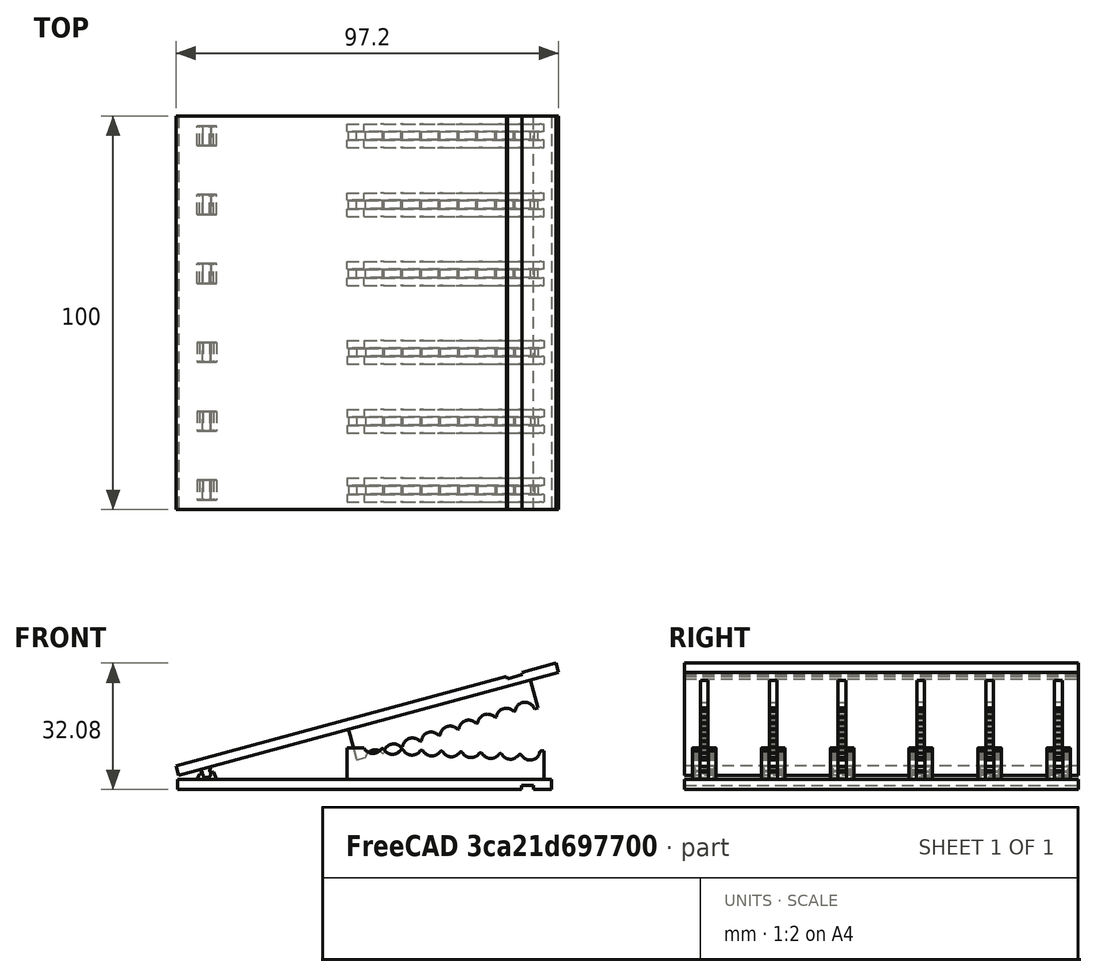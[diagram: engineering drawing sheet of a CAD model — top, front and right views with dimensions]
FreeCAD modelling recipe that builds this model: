
FCSTD DOCUMENT  (FreeCAD 2020.12.17R23076 +3024 (Git))
Label: Modular Ramp v3 Simulated
License: All rights reserved
LicenseURL: http://en.wikipedia.org/wiki/All_rights_reserved
objects: Sketcher::SketchObject×12, PartDesign::Pad×6, PartDesign::ShapeBinder×3, PartDesign::Plane×3, PartDesign::Body×3, PartDesign::Pocket×3, PartDesign::LinearPattern×2, PartDesign::Mirrored×2, Spreadsheet::Sheet×1, TechDraw::DrawSVGTemplate×1, TechDraw::DrawPage×1
note: 56 computed .brp shape members not serialized (recipe doc carries the construction recipe); baked Part::Feature solids carry a one-line shape summary decoded from their .brp

FEATURE [Sketcher::SketchObject] Sketch
  MapMode = 5
  Placement = pos=(0,0,0) rot=(1,0,0;1.5708rad)
  Support = -> [XZ_Plane]
  expr: Constraints[13] = Spreadsheet.ThicknessLower
  expr: Constraints[179] = Spreadsheet.ThicknessUpper
  expr: Constraints[38] = Spreadsheet.ThicknessUpper + Spreadsheet.ThicknessLower + 3
  sketch-geometry (76):
    g0: LineSegment [constr] StartX=0 StartY=0 StartZ=0 EndX=-10 EndY=0 EndZ=0
    g1: LineSegment StartX=0 StartY=0 StartZ=0 EndX=95 EndY=0 EndZ=0
    g2: LineSegment [constr] StartX=0 StartY=0 StartZ=0 EndX=95 EndY=0 EndZ=0
    g3: LineSegment StartX=95 StartY=0 StartZ=0 EndX=95 EndY=2.5 EndZ=0
    g4: LineSegment StartX=95 StartY=2.5 StartZ=0 EndX=0 EndY=2.5 EndZ=0
    g5: LineSegment StartX=0 StartY=2.5 StartZ=0 EndX=0 EndY=0 EndZ=0
    g6: Circle [constr] CenterX=0 CenterY=2.5 CenterZ=0 NormalX=0 NormalY=0 NormalZ=1 AngleXU=0 Radius=7.5
    g7: LineSegment StartX=-0.136062 StartY=6.99696 StartZ=0 EndX=98.9094 EndY=20.7806 EndZ=0
    g8: LineSegment StartX=98.9094 StartY=20.7806 StartZ=0 EndX=99.254 EndY=18.3045 EndZ=0
    g9: LineSegment StartX=99.254 StartY=18.3045 StartZ=0 EndX=0.208529 EndY=4.52083 EndZ=0
    g10: LineSegment StartX=0.208529 StartY=4.52083 StartZ=0 EndX=-0.136062 EndY=6.99696 EndZ=0
    g11: Circle [constr] CenterX=7.34847 CenterY=4 CenterZ=0 NormalX=0 NormalY=0 NormalZ=1 AngleXU=0 Radius=4
    g12: Circle CenterX=7.34847 CenterY=4 CenterZ=0 NormalX=0 NormalY=0 NormalZ=1 AngleXU=0 Radius=1
    g13: LineSegment [constr] StartX=7.34847 StartY=4 StartZ=0 EndX=6.79712 EndY=7.96182 EndZ=0
    g14: LineSegment [constr] StartX=7.34847 StartY=4 StartZ=0 EndX=7.34847 EndY=0 EndZ=0
    g15: LineSegment StartX=91.9757 StartY=17.2916 StartZ=0 EndX=92.9819 EndY=10.0613 EndZ=0
    g16: LineSegment [constr] StartX=92.9819 StartY=10.0613 StartZ=0 EndX=45.775 EndY=1.3715 EndZ=0
    g17: LineSegment StartX=45.775 StartY=1.3715 StartZ=0 EndX=44.4794 EndY=10.6818 EndZ=0
    g18: LineSegment StartX=45.046 StartY=2.5 StartZ=0 EndX=45.046 EndY=11.9 EndZ=0
    g19: LineSegment [constr] StartX=45.046 StartY=11.9 StartZ=0 EndX=93 EndY=9.8 EndZ=0
    g20: LineSegment StartX=93 StartY=9.8 StartZ=0 EndX=93 EndY=2.5 EndZ=0
    g21: ArcOfCircle CenterX=89.5034 CenterY=9.95312 CenterZ=0 NormalX=0 NormalY=0 NormalZ=1 AngleXU=0 Radius=2.5 StartAngle=3.71237 EndAngle=6.05543
    g22: ArcOfCircle CenterX=89.5397 CenterY=9.42765 CenterZ=0 NormalX=0 NormalY=0 NormalZ=1 AngleXU=0 Radius=2.5 StartAngle=0.182041 EndAngle=2.91212
    g23: GeomPoint X=91.9984 Y=9.88024 Z=0
    g24: GeomPoint X=92.001 Y=9.84375 Z=0
    g25: ArcOfCircle CenterX=84.6224 CenterY=8.52246 CenterZ=0 NormalX=0 NormalY=0 NormalZ=1 AngleXU=0 Radius=2.5 StartAngle=0.593558 EndAngle=2.91212
    g26: Circle [constr] CenterX=7.34847 CenterY=4 CenterZ=0 NormalX=0 NormalY=0 NormalZ=1 AngleXU=0 Radius=85.6647
    g27: ArcOfCircle CenterX=84.5081 CenterY=10.1719 CenterZ=0 NormalX=0 NormalY=0 NormalZ=1 AngleXU=0 Radius=2.5 StartAngle=3.71237 EndAngle=5.62488
    g28: ArcOfCircle CenterX=79.5129 CenterY=10.3906 CenterZ=0 NormalX=0 NormalY=0 NormalZ=1 AngleXU=0 Radius=2.5 StartAngle=3.71237 EndAngle=5.62488
    g29: ArcOfCircle CenterX=74.5177 CenterY=10.6094 CenterZ=0 NormalX=0 NormalY=0 NormalZ=1 AngleXU=0 Radius=2.5 StartAngle=3.71237 EndAngle=5.62488
    g30: ArcOfCircle CenterX=64.5273 CenterY=11.0469 CenterZ=0 NormalX=0 NormalY=0 NormalZ=1 AngleXU=0 Radius=2.5 StartAngle=3.71237 EndAngle=5.62488
    g31: ArcOfCircle CenterX=59.5321 CenterY=11.2656 CenterZ=0 NormalX=0 NormalY=0 NormalZ=1 AngleXU=0 Radius=2.5 StartAngle=3.71237 EndAngle=5.62488
    g32: ArcOfCircle CenterX=54.5369 CenterY=11.4844 CenterZ=0 NormalX=0 NormalY=0 NormalZ=1 AngleXU=0 Radius=2.5 StartAngle=3.71237 EndAngle=5.62488
    g33: ArcOfCircle CenterX=69.5225 CenterY=10.8281 CenterZ=0 NormalX=0 NormalY=0 NormalZ=1 AngleXU=0 Radius=2.5 StartAngle=3.71237 EndAngle=5.62488
    g34: ArcOfCircle CenterX=79.705 CenterY=7.61728 CenterZ=0 NormalX=0 NormalY=0 NormalZ=1 AngleXU=0 Radius=2.5 StartAngle=0.593558 EndAngle=2.91212
    g35: ArcOfCircle CenterX=74.7876 CenterY=6.71209 CenterZ=0 NormalX=0 NormalY=0 NormalZ=1 AngleXU=0 Radius=2.5 StartAngle=0.593558 EndAngle=2.91212
    g36: ArcOfCircle CenterX=69.8702 CenterY=5.80691 CenterZ=0 NormalX=0 NormalY=0 NormalZ=1 AngleXU=0 Radius=2.5 StartAngle=0.593558 EndAngle=2.91212
    g37: ArcOfCircle CenterX=64.9528 CenterY=4.90172 CenterZ=0 NormalX=0 NormalY=0 NormalZ=1 AngleXU=0 Radius=2.5 StartAngle=0.593558 EndAngle=2.91212
    g38: ArcOfCircle CenterX=60.0355 CenterY=3.99654 CenterZ=0 NormalX=0 NormalY=0 NormalZ=1 AngleXU=0 Radius=2.5 StartAngle=0.593558 EndAngle=2.91212
    g39: ArcOfCircle CenterX=55.1181 CenterY=3.09135 CenterZ=0 NormalX=0 NormalY=0 NormalZ=1 AngleXU=0 Radius=2.5 StartAngle=0.593558 EndAngle=2.91212
    g40: ArcOfCircle CenterX=50.2007 CenterY=2.18617 CenterZ=0 NormalX=0 NormalY=0 NormalZ=1 AngleXU=0 Radius=2.5 StartAngle=0.593558 EndAngle=3.32363
    g41: ArcOfCircle CenterX=49.5417 CenterY=11.7031 CenterZ=0 NormalX=0 NormalY=0 NormalZ=1 AngleXU=0 Radius=2.5 StartAngle=3.28182 EndAngle=5.62488
    g42: Circle [constr] CenterX=7.34847 CenterY=4 CenterZ=0 NormalX=0 NormalY=0 NormalZ=1 AngleXU=0 Radius=82.3703
    g43: Circle [constr] CenterX=7.34847 CenterY=4 CenterZ=0 NormalX=0 NormalY=0 NormalZ=1 AngleXU=0 Radius=77.4061
    g44: Circle [constr] CenterX=7.34847 CenterY=4 CenterZ=0 NormalX=0 NormalY=0 NormalZ=1 AngleXU=0 Radius=72.4469
    g45: Circle [constr] CenterX=7.34847 CenterY=4 CenterZ=0 NormalX=0 NormalY=0 NormalZ=1 AngleXU=0 Radius=67.4936
    g46: Circle [constr] CenterX=7.34847 CenterY=4 CenterZ=0 NormalX=0 NormalY=0 NormalZ=1 AngleXU=0 Radius=62.5478
    g47: Circle [constr] CenterX=7.34847 CenterY=4 CenterZ=0 NormalX=0 NormalY=0 NormalZ=1 AngleXU=0 Radius=57.6114
    g48: Circle [constr] CenterX=7.34847 CenterY=4 CenterZ=0 NormalX=0 NormalY=0 NormalZ=1 AngleXU=0 Radius=52.687
    g49: Circle [constr] CenterX=7.34847 CenterY=4 CenterZ=0 NormalX=0 NormalY=0 NormalZ=1 AngleXU=0 Radius=47.7782
    g50: Circle [constr] CenterX=7.34847 CenterY=4 CenterZ=0 NormalX=0 NormalY=0 NormalZ=1 AngleXU=0 Radius=42.8906
    g51: ArcOfCircle CenterX=51.9621 CenterY=9.83121 CenterZ=0 NormalX=0 NormalY=0 NormalZ=1 AngleXU=0 Radius=0.559823 StartAngle=0.570773 EndAngle=2.48329
    g52: ArcOfCircle CenterX=56.9573 CenterY=9.61246 CenterZ=0 NormalX=0 NormalY=0 NormalZ=1 AngleXU=0 Radius=0.559823 StartAngle=0.570773 EndAngle=2.48329
    g53: ArcOfCircle CenterX=92.4842 CenterY=9.26223 CenterZ=0 NormalX=0 NormalY=0 NormalZ=1 AngleXU=0 Radius=0.559823 StartAngle=1.52703 EndAngle=2.91383
    g54: ArcOfCircle CenterX=86.9286 CenterY=8.29996 CenterZ=0 NormalX=0 NormalY=0 NormalZ=1 AngleXU=0 Radius=0.559823 StartAngle=0.570773 EndAngle=2.48329
    g55: ArcOfCircle CenterX=81.9333 CenterY=8.51871 CenterZ=0 NormalX=0 NormalY=0 NormalZ=1 AngleXU=0 Radius=0.559823 StartAngle=0.570773 EndAngle=2.48329
    g56: ArcOfCircle CenterX=76.9381 CenterY=8.73746 CenterZ=0 NormalX=0 NormalY=0 NormalZ=1 AngleXU=0 Radius=0.559823 StartAngle=0.570773 EndAngle=2.48329
    g57: ArcOfCircle CenterX=71.9429 CenterY=8.95621 CenterZ=0 NormalX=0 NormalY=0 NormalZ=1 AngleXU=0 Radius=0.559823 StartAngle=0.570773 EndAngle=2.48329
    g58: ArcOfCircle CenterX=61.9525 CenterY=9.39371 CenterZ=0 NormalX=0 NormalY=0 NormalZ=1 AngleXU=0 Radius=0.559823 StartAngle=0.570773 EndAngle=2.48329
    g59: ArcOfCircle CenterX=66.9477 CenterY=9.17496 CenterZ=0 NormalX=0 NormalY=0 NormalZ=1 AngleXU=0 Radius=0.559823 StartAngle=0.570773 EndAngle=2.48329
    g60: ArcOfCircle CenterX=46.5119 CenterY=11.2754 CenterZ=0 NormalX=0 NormalY=0 NormalZ=1 AngleXU=0 Radius=0.559823 StartAngle=0.140232 EndAngle=1.52703
    g61: LineSegment StartX=92.5086 StartY=9.82152 StartZ=0 EndX=93 EndY=9.8 EndZ=0
    g62: LineSegment StartX=46.5364 StartY=11.8347 StartZ=0 EndX=45.046 EndY=11.9 EndZ=0
    g63: LineSegment StartX=47.742 StartY=1.73357 StartZ=0 EndX=45.775 EndY=1.3715 EndZ=0
    g64: LineSegment StartX=91.9984 StartY=9.88024 StartZ=0 EndX=92.9819 EndY=10.0613 EndZ=0
    g65: LineSegment [constr] StartX=50.2007 StartY=2.18617 StartZ=0 EndX=50.0197 EndY=3.16964 EndZ=0
    g66: LineSegment [constr] StartX=89.3587 StartY=10.4111 StartZ=0 EndX=89.5397 EndY=9.42765 EndZ=0
    g67: LineSegment [constr] StartX=89.3587 StartY=10.4111 StartZ=0 EndX=50.0197 EndY=3.16964 EndZ=0
    g68: LineSegment StartX=52.2731 StartY=3.58445 StartZ=0 EndX=52.6836 EndY=3.66002 EndZ=0
    g69: LineSegment StartX=57.1905 StartY=4.48964 StartZ=0 EndX=57.601 EndY=4.56521 EndZ=0
    g70: LineSegment StartX=62.1078 StartY=5.39482 StartZ=0 EndX=62.5184 EndY=5.47039 EndZ=0
    g71: LineSegment StartX=67.0252 StartY=6.30001 StartZ=0 EndX=67.4357 EndY=6.37558 EndZ=0
    g72: LineSegment StartX=71.9426 StartY=7.20519 StartZ=0 EndX=72.3531 EndY=7.28076 EndZ=0
    g73: LineSegment StartX=76.86 StartY=8.11038 StartZ=0 EndX=77.2705 EndY=8.18595 EndZ=0
    g74: LineSegment StartX=81.7774 StartY=9.01556 StartZ=0 EndX=82.1879 EndY=9.09113 EndZ=0
    g75: LineSegment StartX=86.6947 StartY=9.92075 StartZ=0 EndX=87.1053 EndY=9.99632 EndZ=0
  constraints (239):
    c: Coincident(g0,g-1)
    c: PointOnObject(g0,g-1)
    c: Coincident(g1,g-1)
    c: Horizontal(g1)
    c: DistanceX(g1,g1) = 95
    c: Coincident(g2,g3)
    c: Coincident(g3,g4)
    c: Coincident(g4,g5)
    c: Coincident(g5,g2)
    c: Horizontal(g4)
    c: Vertical(g3)
    c: Vertical(g5)
    c: Coincident(g2,g1)
    c: DistanceY(g3,g3) = 2.5
    c: Coincident(g2,g1)
    c: Coincident(g6,g4)
    c: Diameter(g6) = 15
    c: DistanceX(g0,g0) = 10
    c: Distance(g7) = 100
    c: Coincident(g8,g7)
    c: Coincident(g9,g8)
    c: Coincident(g10,g9)
    c: Coincident(g10,g7)
    c: Perpendicular(g7,g10)
    c: Perpendicular(g8,g9)
    c: Perpendicular(g7,g8)
    c: PointOnObject(g11,g6)
    c: Tangent(g11,g7)
    c: Tangent(g11,g1)
    c: Coincident(g12,g11)
    c: Diameter(g12) = 2
    c: Coincident(g13,g12)
    c: PointOnObject(g13,g7)
    c: Coincident(g14,g12)
    c: PointOnObject(g14,g1)
    c: Perpendicular(g7,g13)
    c: Perpendicular(g1,g14)
    c: Distance(g13,g7) = 7
    c: Diameter(g11) = 8
    c: DistanceY(g1,g7) = 20.7806
    c: PointOnObject(g15,g9)
    c: Coincident(g15,g16)
    c: Coincident(g16,g17)
    c: PointOnObject(g17,g9)
    c: PointOnObject(g18,g4)
    c: Vertical(g18)
    c: Coincident(g18,g19)
    c: Coincident(g19,g20)
    c: PointOnObject(g20,g4)
    c: Perpendicular(g9,g17)
    c: Perpendicular(g4,g20)
    c: Perpendicular(g9,g15)
    c: Equal(g17,g18)
    c: Equal(g20,g15)
    c: Distance(g20,g3) = 2
    c: Distance(g16) = 48
    c: Equal(g16,g19)
    c: Distance(g20) = 7.3
    c: PointOnObject(g21,g19)
    c: PointOnObject(g22,g16)
    c: Diameter(g21) = 5
    c: Equal(g22,g21)
    c: PointOnObject(g23,g22)
    c: PointOnObject(g24,g21)
    c: PointOnObject(g23,g16)
    c: PointOnObject(g24,g19)
    c: Distance(g24,g19) = 1
    c: PointOnObject(g25,g16)
    c: Equal(g22,g25)
    c: Coincident(g26,g12)
    c: PointOnObject(g20,g26)
    c: PointOnObject(g15,g26)
    c: Distance(g18) = 9.4
    c: Equal(g21,g27) = 2
    c: PointOnObject(g27,g19)
    c: Equal(g21,g28) = 2
    c: Equal(g28,g29) = 2
    c: PointOnObject(g29,g19)
    c: PointOnObject(g28,g19)
    c: Equal(g21,g33) = 5
    c: Equal(g33,g30) = 2
    c: Equal(g33,g31) = 2
    c: Equal(g31,g32) = 2
    c: PointOnObject(g33,g19)
    c: Equal(g34,g35)
    c: PointOnObject(g35,g16)
    c: PointOnObject(g30,g19)
    c: PointOnObject(g31,g19)
    c: PointOnObject(g32,g19)
    c: PointOnObject(g34,g16)
    c: Equal(g34,g25)
    c: Equal(g36,g37)
    c: Equal(g38,g39)
    c: Equal(g38,g37)
    c: PointOnObject(g39,g16)
    c: PointOnObject(g38,g16)
    c: PointOnObject(g37,g16)
    c: PointOnObject(g36,g16)
    c: Equal(g36,g35)
    c: PointOnObject(g40,g16)
    c: PointOnObject(g41,g19)
    c: Equal(g39,g40)
    c: Equal(g32,g41)
    c: Coincident(g42,g12)
    c: PointOnObject(g21,g42)
    c: PointOnObject(g22,g42)
    c: Coincident(g43,g12)
    c: PointOnObject(g27,g43)
    c: Coincident(g44,g12)
    c: PointOnObject(g28,g44)
    c: Coincident(g45,g12)
    c: PointOnObject(g29,g45)
    c: Coincident(g46,g12)
    c: PointOnObject(g33,g46)
    c: Coincident(g47,g12)
    c: PointOnObject(g30,g47)
    c: Coincident(g48,g12)
    c: PointOnObject(g31,g48)
    c: Coincident(g49,g12)
    c: PointOnObject(g32,g49)
    c: Coincident(g50,g12)
    c: PointOnObject(g41,g50)
    c: Tangent(g51,g41)
    c: Equal(g51,g52)
    c: PointOnObject(g53,g19)
    c: Tangent(g54,g21)
    c: Tangent(g54,g27)
    c: Tangent(g53,g21)
    c: Tangent(g53,g19)
    c: Tangent(g58,g31)
    c: Tangent(g58,g30)
    c: Tangent(g30,g59)
    c: Tangent(g33,g59)
    c: Tangent(g33,g57)
    c: Tangent(g29,g57)
    c: Equal(g52,g58)
    c: Equal(g58,g59)
    c: Equal(g59,g57)
    c: Equal(g57,g56)
    c: Equal(g56,g55)
    c: Equal(g55,g54)
    c: Equal(g54,g53)
    c: Tangent(g55,g27)
    c: Tangent(g55,g28)
    c: Tangent(g56,g28)
    c: Tangent(g56,g29)
    c: Tangent(g52,g31)
    c: Tangent(g52,g32)
    c: Tangent(g51,g32)
    c: PointOnObject(g60,g19)
    c: Tangent(g60,g41)
    c: Tangent(g60,g19)
    c: Equal(g60,g51)
    c: Coincident(g41,g51)
    c: Coincident(g32,g51)
    c: Coincident(g32,g52)
    c: Coincident(g31,g52)
    c: Coincident(g30,g58)
    c: Coincident(g31,g58)
    c: Coincident(g30,g59)
    c: Coincident(g33,g59)
    c: Coincident(g33,g57)
    c: Coincident(g29,g57)
    c: Coincident(g29,g56)
    c: Coincident(g28,g56)
    c: Coincident(g28,g55)
    c: Coincident(g27,g55)
    c: Coincident(g27,g54)
    c: Coincident(g21,g54)
    c: Coincident(g21,g53)
    c: Distance(g21,g27) = 5
    c: Distance(g27,g28) = 5
    c: Distance(g28,g29) = 5
    c: Distance(g33,g29) = 5
    c: Distance(g33,g30) = 5
    c: Distance(g30,g31) = 5
    c: Distance(g31,g32) = 5
    c: Distance(g32,g41) = 5
    c: Coincident(g41,g60)
    c: Distance(g8) = 2.5
    c: Coincident(g61,g53)
    c: Coincident(g62,g60)
    c: Coincident(g61,g20)
    c: Coincident(g62,g18)
    c: PointOnObject(g22,g16)
    c: PointOnObject(g40,g16)
    c: Coincident(g63,g40)
    c: Coincident(g63,g17)
    c: Coincident(g64,g22)
    c: Coincident(g64,g15)
    c: Coincident(g65,g40)
    c: Coincident(g66,g22)
    c: Coincident(g67,g66)
    c: Coincident(g67,g65)
    c: Perpendicular(g65,g67)
    c: Perpendicular(g66,g67)
    c: Parallel(g67,g16)
    c: Distance(g66,g22) = 1
    c: PointOnObject(g25,g43)
    c: PointOnObject(g34,g44)
    c: PointOnObject(g35,g45)
    c: PointOnObject(g36,g46)
    c: PointOnObject(g37,g47)
    c: PointOnObject(g38,g48)
    c: PointOnObject(g39,g49)
    c: PointOnObject(g40,g50)
    c: PointOnObject(g22,g67)
    c: PointOnObject(g25,g67)
    c: PointOnObject(g25,g67)
    c: PointOnObject(g34,g67)
    c: PointOnObject(g34,g67)
    c: PointOnObject(g35,g67)
    c: PointOnObject(g39,g67)
    c: PointOnObject(g40,g67)
    c: PointOnObject(g38,g67)
    c: PointOnObject(g39,g67)
    c: PointOnObject(g37,g67)
    c: PointOnObject(g38,g67)
    c: PointOnObject(g37,g67)
    c: PointOnObject(g36,g67)
    c: PointOnObject(g35,g67)
    c: PointOnObject(g36,g67)
    c: Distance(g15) = 7.3
    c: Coincident(g68,g40)
    c: Coincident(g68,g39)
    c: Coincident(g69,g39)
    c: Coincident(g69,g38)
    c: Coincident(g70,g38)
    c: Coincident(g70,g37)
    c: Coincident(g71,g37)
    c: Coincident(g71,g36)
    c: Coincident(g72,g36)
    c: Coincident(g72,g35)
    c: Coincident(g73,g35)
    c: Coincident(g73,g34)
    c: Coincident(g74,g34)
    c: Coincident(g74,g25)
    c: Coincident(g75,g25)
    c: Coincident(g75,g22)
FEATURE [Sketcher::SketchObject] Sketch001
  MapMode = 5
  Placement = pos=(0,0,0) rot=(1,0,0;1.5708rad)
  Support = -> [XZ_Plane001]
  expr: Constraints[11] = Sketch.Constraints[13]
  expr: Constraints[2] = Sketch.Constraints[4]
  sketch-geometry (5):
    g0: LineSegment StartX=0 StartY=0 StartZ=0 EndX=95 EndY=0 EndZ=0
    g1: LineSegment [constr] StartX=0 StartY=0 StartZ=0 EndX=95 EndY=0 EndZ=0
    g2: LineSegment StartX=95 StartY=0 StartZ=0 EndX=95 EndY=2.5 EndZ=0
    g3: LineSegment StartX=95 StartY=2.5 StartZ=0 EndX=0 EndY=2.5 EndZ=0
    g4: LineSegment StartX=0 StartY=2.5 StartZ=0 EndX=0 EndY=0 EndZ=0
  constraints (13):
    c: Coincident(g0,g-1)
    c: Horizontal(g0)
    c: DistanceX(g0,g0) = 95
    c: Coincident(g1,g2)
    c: Coincident(g2,g3)
    c: Coincident(g3,g4)
    c: Coincident(g4,g1)
    c: Horizontal(g3)
    c: Vertical(g2)
    c: Vertical(g4)
    c: Coincident(g1,g0)
    c: DistanceY(g2,g2) = 2.5
    c: Coincident(g1,g0)
FEATURE [Spreadsheet::Sheet] Spreadsheet
  PythonMode = false
  cells = A1=DepthOfPad; B1(DepthOfPad)==100mm; A2=ThicknessUpper; B2(ThicknessUpper)==2.5mm; A3=ThicknessLower; B3(ThicknessLower)==2.5mm; A4=ThicknessRibTop; B4(ThicknessRibTop)==2mm; A5=ThicknessSwivel; B5(ThicknessSwivel)==5mm
FEATURE [PartDesign::Pad] Pad
  ClaimChildren = false
  Direction = (1,1,1)
  Fit = 0
  FitJoin = 0
  InnerFit = 0
  InnerFitJoin = 0
  InnerTaperAngle = 0
  InnerTaperAngleRev = 0
  Length = 100
  Length2 = 100
  Midplane = true
  NewSolid = false
  Placement = pos=(0,0,0) rot=(1,0,0;1.5708rad)
  Profile = -> Sketch001
  Suppress = false
  Type = 0
  expr: Length = Spreadsheet.DepthOfPad
FEATURE [PartDesign::ShapeBinder] ShapeBinder
  Support = -> [Sketch]
  TraceSupport = false
FEATURE [Sketcher::SketchObject] Sketch003
  ExternalGeometry = -> [ShapeBinder]
  MapMode = 5
  Placement = pos=(0,0,0) rot=(1,0,0;1.5708rad)
  Support = -> [XZ_Plane002]
FEATURE [PartDesign::Pad] Pad002
  ClaimChildren = false
  Direction = (1,1,1)
  Fit = 0
  FitJoin = 0
  InnerFit = 0
  InnerFitJoin = 0
  InnerTaperAngle = 0
  InnerTaperAngleRev = 0
  Length = 100
  Length2 = 100
  Midplane = true
  NewSolid = false
  Placement = pos=(0,0,0) rot=(1,0,0;1.5708rad)
  Profile = -> Sketch003
  Suppress = false
  Type = 0
  expr: Length = Spreadsheet.DepthOfPad
FEATURE [PartDesign::Plane] DatumPlane
  AttachmentOffset = pos=(0,0,10) rot=(0,0,1;0rad)
  Length = 95.7082
  MapMode = 5
  MinimumLength = 10
  MinimumWidth = 10
  Placement = pos=(0,-10,-2.2e-15) rot=(1,0,0;1.5708rad)
  ResizeMode = 0
  Support = -> [XZ_Plane]
  Width = 56.5141
FEATURE [PartDesign::Body] Body
  ExportMode = 0
  Group = -> [Sketch,DatumPlane]
  Origin = -> Origin
  _ExportChildren = -> [Sketch,DatumPlane]
  _GroupVersion = 1
FEATURE [PartDesign::Plane] ReferenceDatumPlane
  Length = 60
  MapMode = 5
  MinimumLength = 10
  MinimumWidth = 10
  Placement = pos=(0,-10,-2.2e-15) rot=(1,0,0;1.5708rad)
  ResizeMode = 0
  Support = -> [DatumPlane]
  Width = 10
FEATURE [Sketcher::SketchObject] Sketch004
  MapMode = 5
  Placement = pos=(0,-10,-2.2e-15) rot=(1,0,0;1.5708rad)
  Support = -> [DatumPlane]
  expr: Constraints[13] = Sketch.Constraints[13]
  expr: Constraints[16] = Sketch.Constraints[16]
  expr: Constraints[17] = Sketch.Constraints[17]
  expr: Constraints[18] = Sketch.Constraints[18]
  expr: Constraints[30] = Sketch.Constraints[30]
  expr: Constraints[37] = Sketch.Constraints[37]
  expr: Constraints[38] = Sketch.Constraints[38]
  expr: Constraints[40] = Sketch.Constraints[179]
  expr: Constraints[4] = Sketch.Constraints[4]
  sketch-geometry (26):
    g0: LineSegment [constr] StartX=0 StartY=0 StartZ=0 EndX=-10 EndY=0 EndZ=0
    g1: LineSegment [constr] StartX=0 StartY=0 StartZ=0 EndX=95 EndY=0 EndZ=0
    g2: LineSegment [constr] StartX=0 StartY=0 StartZ=0 EndX=95 EndY=0 EndZ=0
    g3: LineSegment [constr] StartX=95 StartY=0 StartZ=0 EndX=95 EndY=2.5 EndZ=0
    g4: LineSegment [constr] StartX=95 StartY=2.5 StartZ=0 EndX=0 EndY=2.5 EndZ=0
    g5: LineSegment [constr] StartX=0 StartY=2.5 StartZ=0 EndX=0 EndY=0 EndZ=0
    g6: Circle [constr] CenterX=0 CenterY=2.5 CenterZ=0 NormalX=0 NormalY=0 NormalZ=1 AngleXU=0 Radius=7.5
    g7: LineSegment [constr] StartX=-0.673992 StartY=4.80007 StartZ=0 EndX=90.6453 EndY=45.5529 EndZ=0
    g8: LineSegment [constr] StartX=90.6453 StartY=45.5529 StartZ=0 EndX=91.6641 EndY=43.2699 EndZ=0
    g9: LineSegment [constr] StartX=91.6641 StartY=43.2699 StartZ=0 EndX=0.344828 EndY=2.51709 EndZ=0
    g10: LineSegment [constr] StartX=0.344828 StartY=2.51709 StartZ=0 EndX=-0.673992 EndY=4.80007 EndZ=0
    g11: Circle [constr] CenterX=7.34847 CenterY=4 CenterZ=0 NormalX=0 NormalY=0 NormalZ=1 AngleXU=0 Radius=4
    g12: Circle [constr] CenterX=7.34847 CenterY=4 CenterZ=0 NormalX=0 NormalY=0 NormalZ=1 AngleXU=0 Radius=1
    g13: LineSegment [constr] StartX=7.34847 StartY=4 StartZ=0 EndX=5.71836 EndY=7.65277 EndZ=0
    g14: LineSegment [constr] StartX=7.34847 StartY=4 StartZ=0 EndX=7.34847 EndY=0 EndZ=0
    g15: ArcOfCircle CenterX=7.34847 CenterY=4 CenterZ=0 NormalX=0 NormalY=0 NormalZ=1 AngleXU=0 Radius=1.05 StartAngle=3.08957 EndAngle=6.61446
    g16: LineSegment StartX=9.0536 StartY=4.44161 StartZ=0 EndX=9.84847 EndY=2.5 EndZ=0
    g17: LineSegment StartX=9.84847 StartY=2.5 StartZ=0 EndX=7.34847 EndY=2.5 EndZ=0
    g18: LineSegment StartX=7.34847 StartY=2.5 StartZ=0 EndX=4.84847 EndY=2.5 EndZ=0
    g19: LineSegment StartX=4.84847 StartY=2.5 StartZ=0 EndX=5.58767 EndY=3.9545 EndZ=0
    g20: LineSegment StartX=5.58767 StartY=3.9545 StartZ=0 EndX=6.29989 EndY=4.0546 EndZ=0
    g21: LineSegment [constr] StartX=7.34847 StartY=4 StartZ=0 EndX=10.2186 EndY=4.40337 EndZ=0
    g22: LineSegment [constr] StartX=10.4208 StartY=4.63376 StartZ=0 EndX=3.94001 EndY=3.72294 EndZ=0
    g23: LineSegment [constr] StartX=7.34847 StartY=4 StartZ=0 EndX=3.86149 EndY=3.50994 EndZ=0
    g24: LineSegment StartX=8.34138 StartY=4.34151 StartZ=0 EndX=9.0536 EndY=4.44161 EndZ=0
    g25: LineSegment [constr] StartX=7.34847 StartY=4 StartZ=0 EndX=7.32063 EndY=4.19805 EndZ=0
  constraints (71):
    c: Coincident(g0,g-1)
    c: PointOnObject(g0,g-1)
    c: Coincident(g1,g-1)
    c: Horizontal(g1)
    c: DistanceX(g1,g1) = 95
    c: Coincident(g2,g3)
    c: Coincident(g3,g4)
    c: Coincident(g4,g5)
    c: Coincident(g5,g2)
    c: Horizontal(g4)
    c: Vertical(g3)
    c: Vertical(g5)
    c: Coincident(g2,g1)
    c: DistanceY(g3,g3) = 2.5
    c: Coincident(g2,g1)
    c: Coincident(g6,g4)
    c: Diameter(g6) = 15
    c: DistanceX(g0,g0) = 10
    c: Distance(g7) = 100
    c: Coincident(g8,g7)
    c: Coincident(g9,g8)
    c: Coincident(g10,g9)
    c: Coincident(g10,g7)
    c: Perpendicular(g7,g10)
    c: Perpendicular(g8,g9)
    c: Perpendicular(g7,g8)
    c: PointOnObject(g11,g6)
    c: Tangent(g11,g7)
    c: Tangent(g11,g1)
    c: Coincident(g12,g11)
    c: Diameter(g12) = 2
    c: Coincident(g13,g12)
    c: PointOnObject(g13,g7)
    c: Coincident(g14,g12)
    c: PointOnObject(g14,g1)
    c: Perpendicular(g7,g13)
    c: Perpendicular(g1,g14)
    c: Distance(g13,g7) = 7
    c: Diameter(g11) = 8
    c: DistanceY(g1,g7) = 45.5529
    c: Distance(g8) = 2.5
    c: Coincident(g15,g11)
    c: Diameter(g15) = 2.1
    c: PointOnObject(g16,g4)
    c: Coincident(g16,g17)
    c: PointOnObject(g17,g4)
    c: Coincident(g17,g18)
    c: PointOnObject(g18,g4)
    c: Coincident(g18,g19)
    c: Coincident(g19,g20)
    c: Coincident(g15,g20)
    c: Equal(g17,g18)
    c: Vertical(g15,g17)
    c: DistanceX(g18,g16) = 5
    c: Coincident(g21,g15)
    c: Coincident(g23,g15)
    c: Parallel(g21,g23)
    c: Parallel(g22,g23)
    c: Parallel(g20,g22)
    c: Coincident(g24,g15)
    c: Coincident(g24,g16)
    c: PointOnObject(g15,g22)
    c: Coincident(g25,g15)
    c: PointOnObject(g25,g22)
    c: Perpendicular(g22,g25)
    c: Distance(g25) = 0.2
    c: Parallel(g22,g24)
    c: PointOnObject(g15,g22)
    c: Distance(g19,g16) = 3.5
    c: Equal(g20,g24)
    c: Angle(g17,g21) = 0.139626
FEATURE [Sketcher::SketchObject] Sketch005
  MapMode = 5
  Placement = pos=(0,-10,-2.2e-15) rot=(1,0,0;1.5708rad)
  Support = -> [DatumPlane]
  expr: Constraints[13] = Sketch.Constraints[13]
  expr: Constraints[16] = Sketch.Constraints[16]
  expr: Constraints[170] = Sketch.Constraints[170]
  expr: Constraints[171] = Sketch.Constraints[171]
  expr: Constraints[172] = Sketch.Constraints[172]
  expr: Constraints[173] = Sketch.Constraints[173]
  expr: Constraints[174] = Sketch.Constraints[174]
  expr: Constraints[175] = Sketch.Constraints[175]
  expr: Constraints[176] = Sketch.Constraints[176]
  expr: Constraints[177] = Sketch.Constraints[179]
  expr: Constraints[17] = Sketch.Constraints[17]
  expr: Constraints[18] = Sketch.Constraints[18]
  expr: Constraints[30] = Sketch.Constraints[30]
  expr: Constraints[37] = Sketch.Constraints[37]
  expr: Constraints[38] = Sketch.Constraints[38]
  expr: Constraints[4] = Sketch.Constraints[4]
  expr: Constraints[54] = Sketch.Constraints[54]
  expr: Constraints[55] = Sketch.Constraints[55]
  expr: Constraints[57] = Sketch.Constraints[57]
  expr: Constraints[60] = Sketch.Constraints[60]
  expr: Constraints[66] = Sketch.Constraints[66]
  expr: Constraints[73] = Sketch.Constraints[72]
  sketch-geometry (64):
    g0: LineSegment [constr] StartX=0 StartY=0 StartZ=0 EndX=-10 EndY=0 EndZ=0
    g1: LineSegment [constr] StartX=0 StartY=0 StartZ=0 EndX=95 EndY=0 EndZ=0
    g2: LineSegment [constr] StartX=0 StartY=0 StartZ=0 EndX=95 EndY=0 EndZ=0
    g3: LineSegment [constr] StartX=95 StartY=0 StartZ=0 EndX=95 EndY=2.5 EndZ=0
    g4: LineSegment [constr] StartX=95 StartY=2.5 StartZ=0 EndX=0 EndY=2.5 EndZ=0
    g5: LineSegment [constr] StartX=0 StartY=2.5 StartZ=0 EndX=0 EndY=0 EndZ=0
    g6: Circle [constr] CenterX=0 CenterY=2.5 CenterZ=0 NormalX=0 NormalY=0 NormalZ=1 AngleXU=0 Radius=7.5
    g7: LineSegment [constr] StartX=-0.587767 StartY=5.41991 StartZ=0 EndX=93.6173 EndY=38.9669 EndZ=0
    g8: LineSegment [constr] StartX=93.6173 StartY=38.9669 StartZ=0 EndX=94.456 EndY=36.6118 EndZ=0
    g9: LineSegment [constr] StartX=94.456 StartY=36.6118 StartZ=0 EndX=0.250908 EndY=3.06478 EndZ=0
    g10: LineSegment [constr] StartX=0.250908 StartY=3.06478 StartZ=0 EndX=-0.587767 EndY=5.41991 EndZ=0
    g11: Circle [constr] CenterX=7.34847 CenterY=4 CenterZ=0 NormalX=0 NormalY=0 NormalZ=1 AngleXU=0 Radius=4
    g12: Circle [constr] CenterX=7.34847 CenterY=4 CenterZ=0 NormalX=0 NormalY=0 NormalZ=1 AngleXU=0 Radius=1
    g13: LineSegment [constr] StartX=7.34847 StartY=4 StartZ=0 EndX=6.00659 EndY=7.7682 EndZ=0
    g14: LineSegment [constr] StartX=7.34847 StartY=4 StartZ=0 EndX=7.34847 EndY=0 EndZ=0
    g15: LineSegment [constr] StartX=87.5334 StartY=34.1466 StartZ=0 EndX=89.9823 EndY=27.2696 EndZ=0
    g16: LineSegment [constr] StartX=89.9823 StartY=27.2696 StartZ=0 EndX=45.5116 EndY=9.20418 EndZ=0
    g17: LineSegment [constr] StartX=45.5116 StartY=9.20418 StartZ=0 EndX=42.3582 EndY=18.0595 EndZ=0
    g18: LineSegment [constr] StartX=45.046 StartY=2.5 StartZ=0 EndX=45.046 EndY=11.9 EndZ=0
    g19: LineSegment [constr] StartX=45.046 StartY=11.9 StartZ=0 EndX=93 EndY=9.8 EndZ=0
    g20: LineSegment StartX=93 StartY=9.8 StartZ=0 EndX=93 EndY=2.5 EndZ=0
    g21: ArcOfCircle CenterX=89.5034 CenterY=9.95313 CenterZ=0 NormalX=0 NormalY=0 NormalZ=1 AngleXU=0 Radius=2.5 StartAngle=3.68351 EndAngle=6.07197
    g22: Circle [constr] CenterX=86.7396 CenterY=25.9524 CenterZ=0 NormalX=0 NormalY=0 NormalZ=1 AngleXU=0 Radius=2.5
    g23: GeomPoint X=89.0558 Y=26.8933 Z=0
    g24: GeomPoint X=92.001 Y=9.84375 Z=0
    g25: Circle [constr] CenterX=82.1073 CenterY=24.0706 CenterZ=0 NormalX=0 NormalY=0 NormalZ=1 AngleXU=0 Radius=2.5
    g26: Circle [constr] CenterX=7.34847 CenterY=4 CenterZ=0 NormalX=0 NormalY=0 NormalZ=1 AngleXU=0 Radius=85.6647
    g27: ArcOfCircle CenterX=84.5081 CenterY=10.1719 CenterZ=0 NormalX=0 NormalY=0 NormalZ=1 AngleXU=0 Radius=2.5 StartAngle=3.68351 EndAngle=5.65374
    g28: ArcOfCircle CenterX=79.5129 CenterY=10.3906 CenterZ=0 NormalX=0 NormalY=0 NormalZ=1 AngleXU=0 Radius=2.5 StartAngle=3.68351 EndAngle=5.65374
    g29: ArcOfCircle CenterX=74.5177 CenterY=10.6094 CenterZ=0 NormalX=0 NormalY=0 NormalZ=1 AngleXU=0 Radius=2.5 StartAngle=3.68351 EndAngle=5.65374
    g30: ArcOfCircle CenterX=64.5273 CenterY=11.0469 CenterZ=0 NormalX=0 NormalY=0 NormalZ=1 AngleXU=0 Radius=2.5 StartAngle=3.68351 EndAngle=5.65374
    g31: ArcOfCircle CenterX=59.5321 CenterY=11.2656 CenterZ=0 NormalX=0 NormalY=0 NormalZ=1 AngleXU=0 Radius=2.5 StartAngle=3.68351 EndAngle=5.65374
    g32: ArcOfCircle CenterX=54.5369 CenterY=11.4844 CenterZ=0 NormalX=0 NormalY=0 NormalZ=1 AngleXU=0 Radius=2.5 StartAngle=3.7117 EndAngle=5.65374
    g33: ArcOfCircle CenterX=69.5225 CenterY=10.8281 CenterZ=0 NormalX=0 NormalY=0 NormalZ=1 AngleXU=0 Radius=2.5 StartAngle=3.68351 EndAngle=5.65374
    g34: Circle [constr] CenterX=77.4749 CenterY=22.1887 CenterZ=0 NormalX=0 NormalY=0 NormalZ=1 AngleXU=0 Radius=2.5
    g35: Circle [constr] CenterX=72.8426 CenterY=20.3069 CenterZ=0 NormalX=0 NormalY=0 NormalZ=1 AngleXU=0 Radius=2.5
    g36: Circle [constr] CenterX=68.2102 CenterY=18.4251 CenterZ=0 NormalX=0 NormalY=0 NormalZ=1 AngleXU=0 Radius=2.5
    g37: Circle [constr] CenterX=63.5778 CenterY=16.5433 CenterZ=0 NormalX=0 NormalY=0 NormalZ=1 AngleXU=0 Radius=2.5
    g38: Circle [constr] CenterX=58.9455 CenterY=14.6615 CenterZ=0 NormalX=0 NormalY=0 NormalZ=1 AngleXU=0 Radius=2.5
    g39: Circle [constr] CenterX=54.3131 CenterY=12.7796 CenterZ=0 NormalX=0 NormalY=0 NormalZ=1 AngleXU=0 Radius=2.5
    g40: Circle [constr] CenterX=49.6808 CenterY=10.8978 CenterZ=0 NormalX=0 NormalY=0 NormalZ=1 AngleXU=0 Radius=2.5
    g41: Circle [constr] CenterX=7.34847 CenterY=4 CenterZ=0 NormalX=0 NormalY=0 NormalZ=1 AngleXU=0 Radius=82.3703
    g42: Circle [constr] CenterX=7.34847 CenterY=4 CenterZ=0 NormalX=0 NormalY=0 NormalZ=1 AngleXU=0 Radius=77.4061
    g43: Circle [constr] CenterX=7.34847 CenterY=4 CenterZ=0 NormalX=0 NormalY=0 NormalZ=1 AngleXU=0 Radius=72.4469
    g44: Circle [constr] CenterX=7.34847 CenterY=4 CenterZ=0 NormalX=0 NormalY=0 NormalZ=1 AngleXU=0 Radius=67.4936
    g45: Circle [constr] CenterX=7.34847 CenterY=4 CenterZ=0 NormalX=0 NormalY=0 NormalZ=1 AngleXU=0 Radius=62.5478
    g46: Circle [constr] CenterX=7.34847 CenterY=4 CenterZ=0 NormalX=0 NormalY=0 NormalZ=1 AngleXU=0 Radius=57.6114
    g47: Circle [constr] CenterX=7.34847 CenterY=4 CenterZ=0 NormalX=0 NormalY=0 NormalZ=1 AngleXU=0 Radius=52.687
    g48: Circle [constr] CenterX=7.34847 CenterY=4 CenterZ=0 NormalX=0 NormalY=0 NormalZ=1 AngleXU=0 Radius=47.7782
    g49: Circle [constr] CenterX=7.34847 CenterY=4 CenterZ=0 NormalX=0 NormalY=0 NormalZ=1 AngleXU=0 Radius=42.8738
    g50: ArcOfCircle CenterX=52.0113 CenterY=9.8652 CenterZ=0 NormalX=0 NormalY=0 NormalZ=1 AngleXU=0 Radius=0.5 StartAngle=0.570112 EndAngle=2.51391
    g51: ArcOfCircle CenterX=56.9619 CenterY=9.71828 CenterZ=0 NormalX=0 NormalY=0 NormalZ=1 AngleXU=0 Radius=0.5 StartAngle=0.541921 EndAngle=2.51214
    g52: ArcOfCircle CenterX=92.4367 CenterY=9.32419 CenterZ=0 NormalX=0 NormalY=0 NormalZ=1 AngleXU=0 Radius=0.5 StartAngle=1.52703 EndAngle=2.93038
    g53: ArcOfCircle CenterX=86.9332 CenterY=8.40578 CenterZ=0 NormalX=0 NormalY=0 NormalZ=1 AngleXU=0 Radius=0.5 StartAngle=0.541921 EndAngle=2.51214
    g54: ArcOfCircle CenterX=81.938 CenterY=8.62453 CenterZ=0 NormalX=0 NormalY=0 NormalZ=1 AngleXU=0 Radius=0.5 StartAngle=0.541923 EndAngle=2.51214
    g55: ArcOfCircle CenterX=76.9428 CenterY=8.84328 CenterZ=0 NormalX=0 NormalY=0 NormalZ=1 AngleXU=0 Radius=0.5 StartAngle=0.541921 EndAngle=2.51214
    g56: ArcOfCircle CenterX=71.9476 CenterY=9.06203 CenterZ=0 NormalX=0 NormalY=0 NormalZ=1 AngleXU=0 Radius=0.5 StartAngle=0.541933 EndAngle=2.51214
    g57: ArcOfCircle CenterX=61.9571 CenterY=9.49953 CenterZ=0 NormalX=0 NormalY=0 NormalZ=1 AngleXU=0 Radius=0.5 StartAngle=0.541922 EndAngle=2.51214
    g58: ArcOfCircle CenterX=66.9523 CenterY=9.28078 CenterZ=0 NormalX=0 NormalY=0 NormalZ=1 AngleXU=0 Radius=0.5 StartAngle=0.541923 EndAngle=2.51214
    g59: LineSegment StartX=92.4586 StartY=9.82371 StartZ=0 EndX=93 EndY=9.8 EndZ=0
    g60: LineSegment StartX=45.046 StartY=2.5 StartZ=0 EndX=93 EndY=2.5 EndZ=0
    g61: LineSegment StartX=45.046 StartY=10.5 StartZ=0 EndX=47.3068 EndY=10.5 EndZ=0
    g62: ArcOfCircle CenterX=49.5597 CenterY=11.627 CenterZ=0 NormalX=0 NormalY=0 NormalZ=1 AngleXU=0 Radius=2.51903 StartAngle=3.60544 EndAngle=5.66098
    g63: LineSegment StartX=45.046 StartY=2.5 StartZ=0 EndX=45.046 EndY=10.5 EndZ=0
  constraints (189):
    c: Coincident(g0,g-1)
    c: PointOnObject(g0,g-1)
    c: Coincident(g1,g-1)
    c: Horizontal(g1)
    c: DistanceX(g1,g1) = 95
    c: Coincident(g2,g3)
    c: Coincident(g3,g4)
    c: Coincident(g4,g5)
    c: Coincident(g5,g2)
    c: Horizontal(g4)
    c: Vertical(g3)
    c: Vertical(g5)
    c: Coincident(g2,g1)
    c: DistanceY(g3,g3) = 2.5
    c: Coincident(g2,g1)
    c: Coincident(g6,g4)
    c: Diameter(g6) = 15
    c: DistanceX(g0,g0) = 10
    c: Distance(g7) = 100
    c: Coincident(g8,g7)
    c: Coincident(g9,g8)
    c: Coincident(g10,g9)
    c: Coincident(g10,g7)
    c: Perpendicular(g7,g10)
    c: Perpendicular(g8,g9)
    c: Perpendicular(g7,g8)
    c: PointOnObject(g11,g6)
    c: Tangent(g11,g7)
    c: Tangent(g11,g1)
    c: Coincident(g12,g11)
    c: Diameter(g12) = 2
    c: Coincident(g13,g12)
    c: PointOnObject(g13,g7)
    c: Coincident(g14,g12)
    c: PointOnObject(g14,g1)
    c: Perpendicular(g7,g13)
    c: Perpendicular(g1,g14)
    c: Distance(g13,g7) = 7
    c: Diameter(g11) = 8
    c: DistanceY(g1,g7) = 38.9669
    c: PointOnObject(g15,g9)
    c: Coincident(g15,g16)
    c: Coincident(g16,g17)
    c: PointOnObject(g17,g9)
    c: PointOnObject(g18,g4)
    c: Vertical(g18)
    c: Coincident(g18,g19)
    c: Coincident(g19,g20)
    c: PointOnObject(g20,g4)
    c: Perpendicular(g9,g17)
    c: Perpendicular(g4,g20)
    c: Perpendicular(g9,g15)
    c: Equal(g17,g18)
    c: Equal(g20,g15)
    c: Distance(g20,g3) = 2
    c: Distance(g16) = 48
    c: Equal(g16,g19)
    c: Distance(g20) = 7.3
    c: PointOnObject(g21,g19)
    c: PointOnObject(g22,g16)
    c: Diameter(g21) = 5
    c: Equal(g22,g21)
    c: PointOnObject(g23,g22)
    c: PointOnObject(g24,g21)
    c: PointOnObject(g23,g16)
    c: PointOnObject(g24,g19)
    c: Distance(g24,g19) = 1
    c: PointOnObject(g25,g16)
    c: Tangent(g25,g22)
    c: Equal(g22,g25)
    c: Coincident(g26,g12)
    c: PointOnObject(g20,g26)
    c: PointOnObject(g15,g26)
    c: Distance(g18) = 9.4
    c: Equal(g21,g27) = 2
    c: PointOnObject(g27,g19)
    c: Equal(g21,g28) = 2
    c: Equal(g28,g29) = 2
    c: PointOnObject(g29,g19)
    c: PointOnObject(g28,g19)
    c: Equal(g21,g33) = 5
    c: Equal(g33,g30) = 2
    c: Equal(g33,g31) = 2
    c: Equal(g31,g32) = 2
    c: PointOnObject(g33,g19)
    c: Tangent(g35,g34)
    c: Equal(g34,g35)
    c: PointOnObject(g35,g16)
    c: Tangent(g34,g25)
    c: PointOnObject(g30,g19)
    c: PointOnObject(g31,g19)
    c: PointOnObject(g32,g19)
    c: PointOnObject(g34,g16)
    c: Equal(g34,g25)
    c: Tangent(g37,g36)
    c: Equal(g36,g37)
    c: Tangent(g39,g38)
    c: Equal(g38,g39)
    c: Tangent(g38,g37)
    c: Equal(g38,g37)
    c: PointOnObject(g39,g16)
    c: PointOnObject(g38,g16)
    c: PointOnObject(g37,g16)
    c: PointOnObject(g36,g16)
    c: Tangent(g36,g35)
    c: Equal(g36,g35)
    c: PointOnObject(g40,g16)
    c: Tangent(g40,g39)
    c: Equal(g39,g40)
    c: Coincident(g41,g12)
    c: PointOnObject(g21,g41)
    c: PointOnObject(g22,g41)
    c: Coincident(g42,g12)
    c: PointOnObject(g27,g42)
    c: Coincident(g43,g12)
    c: PointOnObject(g28,g43)
    c: Coincident(g44,g12)
    c: PointOnObject(g29,g44)
    c: Coincident(g45,g12)
    c: PointOnObject(g33,g45)
    c: Coincident(g46,g12)
    c: PointOnObject(g30,g46)
    c: Coincident(g47,g12)
    c: PointOnObject(g31,g47)
    c: Coincident(g48,g12)
    c: PointOnObject(g32,g48)
    c: Coincident(g49,g12)
    c: Equal(g50,g51)
    c: PointOnObject(g52,g19)
    c: Tangent(g53,g21)
    c: Tangent(g53,g27)
    c: Tangent(g52,g21)
    c: Tangent(g52,g19)
    c: Tangent(g57,g31)
    c: Tangent(g57,g30)
    c: Tangent(g30,g58)
    c: Tangent(g33,g58)
    c: Tangent(g33,g56)
    c: Tangent(g29,g56)
    c: Equal(g51,g57)
    c: Equal(g57,g58)
    c: Equal(g58,g56)
    c: Equal(g56,g55)
    c: Equal(g55,g54)
    c: Equal(g54,g53)
    c: Equal(g53,g52)
    c: Tangent(g54,g27)
    c: Tangent(g54,g28)
    c: Tangent(g55,g28)
    c: Tangent(g55,g29)
    c: Tangent(g51,g31)
    c: Tangent(g51,g32)
    c: Tangent(g50,g32)
    c: Coincident(g62,g50)
    c: Coincident(g32,g50)
    c: Coincident(g32,g51)
    c: Coincident(g31,g51)
    c: Coincident(g30,g57)
    c: Coincident(g31,g57)
    c: Coincident(g30,g58)
    c: Coincident(g33,g58)
    c: Coincident(g33,g56)
    c: Coincident(g29,g56)
    c: Coincident(g29,g55)
    c: Coincident(g28,g55)
    c: Coincident(g28,g54)
    c: Coincident(g27,g54)
    c: Coincident(g27,g53)
    c: Coincident(g21,g53)
    c: Coincident(g21,g52)
    c: Distance(g21,g27) = 5
    c: Distance(g27,g28) = 5
    c: Distance(g28,g29) = 5
    c: Distance(g33,g29) = 5
    c: Distance(g33,g30) = 5
    c: Distance(g30,g31) = 5
    c: Distance(g31,g32) = 5
    c: Distance(g8) = 2.5
    c: Coincident(g59,g52)
    c: Coincident(g59,g20)
    c: Coincident(g60,g18)
    c: Coincident(g60,g20)
    c: Radius(g50) = 0.5
    c: PointOnObject(g61,g18)
    c: DistanceY(g18,g61) = 8
    c: Horizontal(g61)
    c: Coincident(g62,g61)
    c: Coincident(g63,g60)
    c: Coincident(g63,g61)
FEATURE [PartDesign::ShapeBinder] ShapeBinder001
  Placement = pos=(0,0,0) rot=(1,0,0;1.5708rad)
  Support = -> [Sketch]
  TraceSupport = false
FEATURE [Sketcher::SketchObject] Sketch008
  MapMode = 5
  Placement = pos=(0,-10,-2.2e-15) rot=(1,0,0;1.5708rad)
  Support = -> [DatumPlane]
FEATURE [PartDesign::Plane] ReferenceDatumPlane001
  Length = 94.5299
  MapMode = 5
  MinimumLength = 10
  MinimumWidth = 10
  Placement = pos=(0,-10,-2.2e-15) rot=(1,0,0;1.5708rad)
  ResizeMode = 0
  Support = -> [DatumPlane]
  Width = 40.3497
FEATURE [Sketcher::SketchObject] Sketch009
  ExternalGeometry = -> [ShapeBinder001]
  MapMode = 5
  Placement = pos=(0,-10,-2.2e-15) rot=(1,0,0;1.5708rad)
  Support = -> [ReferenceDatumPlane001]
  sketch-geometry (4):
    g0: LineSegment StartX=43.3546 StartY=15.2653 StartZ=0 EndX=89.6541 EndY=27.7534 EndZ=0
    g1: LineSegment StartX=45.438 StartY=7.54136 StartZ=0 EndX=47.6627 EndY=8.14142 EndZ=0
    g2: ArcOfCircle CenterX=50.0919 CenterY=7.55051 CenterZ=0 NormalX=0 NormalY=0 NormalZ=1 AngleXU=0 Radius=2.5 StartAngle=0.718735 EndAngle=2.90297
    g3: LineSegment StartX=43.3546 StartY=15.2653 StartZ=0 EndX=45.438 EndY=7.54136 EndZ=0
  constraints (11):
    c: Coincident(g0,g-3)
    c: Coincident(g0,g-17)
    c: PointOnObject(g1,g-3)
    c: PointOnObject(g1,g-5)
    c: Perpendicular(g-3,g1)
    c: Distance(g1,g0) = 8
    c: Coincident(g2,g-8)
    c: Coincident(g2,g1)
    c: Tangent(g2,g-5)
    c: Coincident(g3,g0)
    c: Coincident(g3,g1)
FEATURE [PartDesign::Pad] Pad005
  BaseFeature = -> Pad002
  ClaimChildren = false
  Direction = (1,1,1)
  Fit = 0
  FitJoin = 0
  InnerFit = 0
  InnerFitJoin = 0
  InnerTaperAngle = 0
  InnerTaperAngleRev = 0
  Length = 2
  Length2 = 100
  Midplane = true
  NewSolid = false
  Placement = pos=(0,0,0) rot=(1,0,0;1.5708rad)
  Profile = -> Sketch009
  Suppress = false
  Type = 0
  expr: Length = Spreadsheet.ThicknessRibTop
FEATURE [Sketcher::SketchObject] Sketch010
  ExternalGeometry = -> [ShapeBinder001,Pad005]
  MapMode = 5
  Placement = pos=(0,-10,-2.2e-15) rot=(1,0,0;1.5708rad)
  Support = -> [ReferenceDatumPlane001]
  sketch-geometry (7):
    g0: LineSegment StartX=6.38212 StartY=4.25722 StartZ=0 EndX=5.5096 EndY=5.05762 EndZ=0
    g1: LineSegment StartX=8.40609 StartY=5.83887 StartZ=0 EndX=5.5096 EndY=5.05762 EndZ=0
    g2: LineSegment StartX=8.40609 StartY=5.83887 StartZ=0 EndX=8.0544 EndY=4.70828 EndZ=0
    g3: LineSegment [constr] StartX=7.34847 StartY=4 StartZ=0 EndX=6.95784 EndY=5.44824 EndZ=0
    g4: ArcOfCircle CenterX=7.34847 CenterY=4 CenterZ=0 NormalX=0 NormalY=0 NormalZ=1 AngleXU=0 Radius=1 StartAngle=2.88145 EndAngle=7.07024
    g5: LineSegment [constr] StartX=8.0544 StartY=4.70828 StartZ=0 EndX=7.21826 EndY=4.48275 EndZ=0
    g6: LineSegment [constr] StartX=7.21826 StartY=4.48275 StartZ=0 EndX=6.38212 EndY=4.25722 EndZ=0
  constraints (19):
    c: PointOnObject(g0,g-3)
    c: Coincident(g1,g0)
    c: Coincident(g2,g1)
    c: PointOnObject(g3,g-4)
    c: Perpendicular(g-4,g3)
    c: PointOnObject(g1,g-4)
    c: Symmetric(g1,g0,g3)
    c: Distance(g0,g1) = 3
    c: Coincident(g4,g2)
    c: Coincident(g4,g0)
    c: Coincident(g5,g2)
    c: PointOnObject(g5,g3)
    c: Perpendicular(g3,g5)
    c: Coincident(g4,g3)
    c: Distance(g5,g3) = 1
    c: Coincident(g6,g5)
    c: Coincident(g6,g0)
    c: Parallel(g5,g6)
    c: Coincident(g4,g-3)
FEATURE [PartDesign::Pad] Pad006
  BaseFeature = -> Pad005
  ClaimChildren = false
  Direction = (1,1,1)
  Fit = 0
  FitJoin = 0
  InnerFit = 0
  InnerFitJoin = 0
  InnerTaperAngle = 0
  InnerTaperAngleRev = 0
  Length = 5
  Length2 = 100
  Midplane = true
  NewSolid = false
  Placement = pos=(0,0,0) rot=(1,0,0;1.5708rad)
  Profile = -> Sketch010
  Suppress = false
  Type = 0
  expr: Length = Spreadsheet.ThicknessSwivel
FEATURE [PartDesign::ShapeBinder] ShapeBinder002
  Placement = pos=(0,0,0) rot=(1,0,0;1.5708rad)
  Support = -> [Sketch]
  TraceSupport = false
FEATURE [Sketcher::SketchObject] Sketch012
  ExternalGeometry = -> [ShapeBinder001,Pad006]
  MapMode = 5
  Placement = pos=(0,-50,-1.1e-14) rot=(1,0,0;1.5708rad)
  Support = -> [Pad006]
  sketch-geometry (5):
    g0: LineSegment StartX=83.5465 StartY=28.6954 StartZ=0 EndX=87.4085 EndY=29.7371 EndZ=0
    g1: LineSegment StartX=87.4085 StartY=29.7371 StartZ=0 EndX=87.5647 EndY=29.1578 EndZ=0
    g2: LineSegment StartX=87.5647 StartY=29.1578 StartZ=0 EndX=83.7027 EndY=28.1161 EndZ=0
    g3: LineSegment StartX=83.7027 StartY=28.1161 StartZ=0 EndX=83.5465 EndY=28.6954 EndZ=0
    g4: LineSegment [constr] StartX=7.34847 StartY=4 StartZ=0 EndX=6.3068 EndY=7.86198 EndZ=0
  constraints (15):
    c: Coincident(g0,g1)
    c: Coincident(g1,g2)
    c: Coincident(g2,g3)
    c: Coincident(g3,g0)
    c: Perpendicular(g3,g0)
    c: Perpendicular(g2,g3)
    c: Perpendicular(g0,g1)
    c: PointOnObject(g0,g-4)
    c: Distance(g0) = 4
    c: Coincident(g4,g-3)
    c: PointOnObject(g4,g-4)
    c: Perpendicular(g-4,g4)
    c: Distance(g4,g0) = 80
    c: PointOnObject(g0,g-4)
    c: Distance(g1) = 0.6
FEATURE [PartDesign::Pocket] Pocket002
  BaseFeature = -> Pad006
  ClaimChildren = false
  Fit = 0
  FitJoin = 0
  InnerFit = 0
  InnerFitJoin = 0
  InnerTaperAngle = 0
  InnerTaperAngleRev = 0
  Length = 5
  Length2 = 100
  NewSolid = false
  Placement = pos=(0,0,0) rot=(1,0,0;1.5708rad)
  Profile = -> Sketch012
  Suppress = false
  Type = 1
FEATURE [PartDesign::LinearPattern] LinearPattern001
  BaseFeature = -> Pocket002
  CopyShape = false
  Direction = -> Y_Axis002
  Length = 35
  NewSolid = false
  Occurrences = 3
  OriginalSubs = -> [Pocket002,Pad006,Pad005]
  Originals = -> [Pocket002,Pad006,Pad005]
  Placement = pos=(0,0,0) rot=(1,0,0;1.5708rad)
  Reversed = true
  SubTransform = true
  Suppress = false
FEATURE [PartDesign::Mirrored] Mirrored
  BaseFeature = -> LinearPattern001
  CopyShape = false
  MirrorPlane = -> XZ_Plane002
  NewSolid = false
  OriginalSubs = -> [LinearPattern001]
  Originals = -> [LinearPattern001]
  Placement = pos=(0,0,0) rot=(1,0,0;1.5708rad)
  SubTransform = true
  Suppress = false
FEATURE [PartDesign::Body] Body002  label="BodyUpper"
  ExportMode = 0
  Group = -> [ShapeBinder,Sketch003,Pad002,ShapeBinder001,Sketch008,ReferenceDatumPlane001,Sketch009,Pad005,Sketch010,Pad006,Sketch012,Pocket002,LinearPattern001,Mirrored]
  Origin = -> Origin002
  Tip = -> Mirrored
  _ExportChildren = -> [ShapeBinder,Pad002,ShapeBinder001,Sketch008,ReferenceDatumPlane001,Pad005,Pad006,Pocket002,LinearPattern001,Mirrored]
  _GroupVersion = 1
FEATURE [TechDraw::DrawSVGTemplate] Template
  EditableTexts = Designed_by_Name=Designed by Name; Drawing_number=Drawing number; FC-Date=Date; FC-SC=Scale; FC-SH=Sheet; FC-Title=Title; Subtitle=Subtitle; Weight=Weight
  Height = 210
  Orientation = 1
  Width = 297
FEATURE [TechDraw::DrawPage] Page
  KeepUpdated = true
  NextBalloonIndex = 1
  ProjectionType = 0
  Template = -> Template
FEATURE [PartDesign::Body] Body001  label="BodyLower"
  ExportMode = 0
  Group = -> [Sketch001,Pad,Sketch004,Pocket001,Pad003,Sketch005,Pad004,Sketch006,Sketch007,Pocket,ShapeBinder002,Sketch011,LinearPattern,Mirrored001]
  Origin = -> Origin001
  Tip = -> Mirrored001
  _ExportChildren = -> [Pad,Pocket001,Pad003,Pad004,Sketch006,Pocket,ShapeBinder002,LinearPattern,Mirrored001]
  _GroupVersion = 1
FEATURE [PartDesign::Pad] Pad003
  BaseFeature = -> Pocket001
  ClaimChildren = false
  Direction = (1,1,1)
  Fit = 0
  FitJoin = 0
  InnerFit = 0
  InnerFitJoin = 0
  InnerTaperAngle = 0
  InnerTaperAngleRev = 0
  Length = 5
  Length2 = 100
  Midplane = true
  NewSolid = false
  Placement = pos=(0,0,0) rot=(1,0,0;1.5708rad)
  Profile = -> Sketch004
  Suppress = false
  Type = 0
  expr: Length = Spreadsheet.ThicknessSwivel
FEATURE [PartDesign::Pad] Pad004
  BaseFeature = -> Pad003
  ClaimChildren = false
  Direction = (1,1,1)
  Fit = 0
  FitJoin = 0
  InnerFit = 0
  InnerFitJoin = 0
  InnerTaperAngle = 0
  InnerTaperAngleRev = 0
  Length = 6
  Length2 = 100
  Midplane = true
  NewSolid = false
  Placement = pos=(0,0,0) rot=(1,0,0;1.5708rad)
  Profile = -> Sketch005
  Suppress = false
  Type = 0
FEATURE [Sketcher::SketchObject] Sketch006
  MapMode = 5
  Placement = pos=(0,0,2.5) rot=(0,0,1;3.14159rad)
  Support = -> [Pad004]
FEATURE [Sketcher::SketchObject] Sketch007
  ExternalGeometry = -> [Pad004]
  MapMode = 5
  Placement = pos=(0,-10,-2.2e-15) rot=(1,0,0;1.5708rad)
  Support = -> [DatumPlane]
  sketch-geometry (4):
    g0: LineSegment StartX=45.046 StartY=2.5 StartZ=0 EndX=93 EndY=2.5 EndZ=0
    g1: LineSegment StartX=93 StartY=2.5 StartZ=0 EndX=93 EndY=10.5 EndZ=0
    g2: LineSegment StartX=93 StartY=10.5 StartZ=0 EndX=45.046 EndY=10.5 EndZ=0
    g3: LineSegment StartX=45.046 StartY=10.5 StartZ=0 EndX=45.046 EndY=2.5 EndZ=0
  constraints (9):
    c: Coincident(g0,g1)
    c: Coincident(g1,g2)
    c: Horizontal(g2)
    c: Vertical(g1)
    c: Coincident(g0,g-4)
    c: Coincident(g2,g-4)
    c: Coincident(g0,g-3)
    c: Coincident(g3,g2)
    c: Coincident(g3,g0)
FEATURE [PartDesign::Pocket] Pocket
  BaseFeature = -> Pad004
  ClaimChildren = false
  Fit = 0
  FitJoin = 0
  InnerFit = 0
  InnerFitJoin = 0
  InnerTaperAngle = 0
  InnerTaperAngleRev = 0
  Length = 2.2
  Length2 = 100
  Midplane = true
  NewSolid = false
  Placement = pos=(0,0,0) rot=(1,0,0;1.5708rad)
  Profile = -> Sketch007
  Suppress = false
  Type = 0
  expr: Length = Spreadsheet.ThicknessRibTop + 0.2
FEATURE [Sketcher::SketchObject] Sketch011
  ExternalGeometry = -> [Pocket,ShapeBinder002]
  MapMode = 5
  Placement = pos=(0,-50,-1.1e-14) rot=(1,0,0;1.5708rad)
  Support = -> [Pocket]
  sketch-geometry (4):
    g0: LineSegment StartX=90.3485 StartY=0 StartZ=0 EndX=87.3485 EndY=0 EndZ=0
    g1: LineSegment StartX=87.3485 StartY=0 StartZ=0 EndX=87.3485 EndY=1 EndZ=0
    g2: LineSegment StartX=87.3485 StartY=1 StartZ=0 EndX=90.3485 EndY=1 EndZ=0
    g3: LineSegment StartX=90.3485 StartY=1 StartZ=0 EndX=90.3485 EndY=0 EndZ=0
  constraints (12):
    c: Coincident(g0,g1)
    c: Coincident(g1,g2)
    c: Coincident(g2,g3)
    c: Coincident(g3,g0)
    c: Horizontal(g0)
    c: Horizontal(g2)
    c: Vertical(g1)
    c: Vertical(g3)
    c: PointOnObject(g0,g-1)
    c: DistanceX(g0,g0) = 3
    c: DistanceX(g-4,g0) = 80
    c: DistanceY(g3,g3) = 1
FEATURE [PartDesign::Pocket] Pocket001
  BaseFeature = -> Pad
  ClaimChildren = false
  Fit = 0
  FitJoin = 0
  InnerFit = 0
  InnerFitJoin = 0
  InnerTaperAngle = 0
  InnerTaperAngleRev = 0
  Length = 5
  Length2 = 100
  NewSolid = false
  Placement = pos=(0,0,0) rot=(1,0,0;1.5708rad)
  Profile = -> Sketch011
  Suppress = false
  Type = 1
FEATURE [PartDesign::LinearPattern] LinearPattern
  BaseFeature = -> Pocket
  CopyShape = false
  Direction = -> Y_Axis001
  Length = 35
  NewSolid = false
  Occurrences = 3
  OriginalSubs = -> [Pocket,Pad004,Pad003]
  Originals = -> [Pocket,Pad004,Pad003]
  Placement = pos=(0,0,0) rot=(1,0,0;1.5708rad)
  Reversed = true
  SubTransform = true
  Suppress = false
FEATURE [PartDesign::Mirrored] Mirrored001
  BaseFeature = -> LinearPattern
  CopyShape = false
  MirrorPlane = -> XZ_Plane001
  NewSolid = false
  OriginalSubs = -> [LinearPattern]
  Originals = -> [LinearPattern]
  Placement = pos=(0,0,0) rot=(1,0,0;1.5708rad)
  SubTransform = true
  Suppress = false
